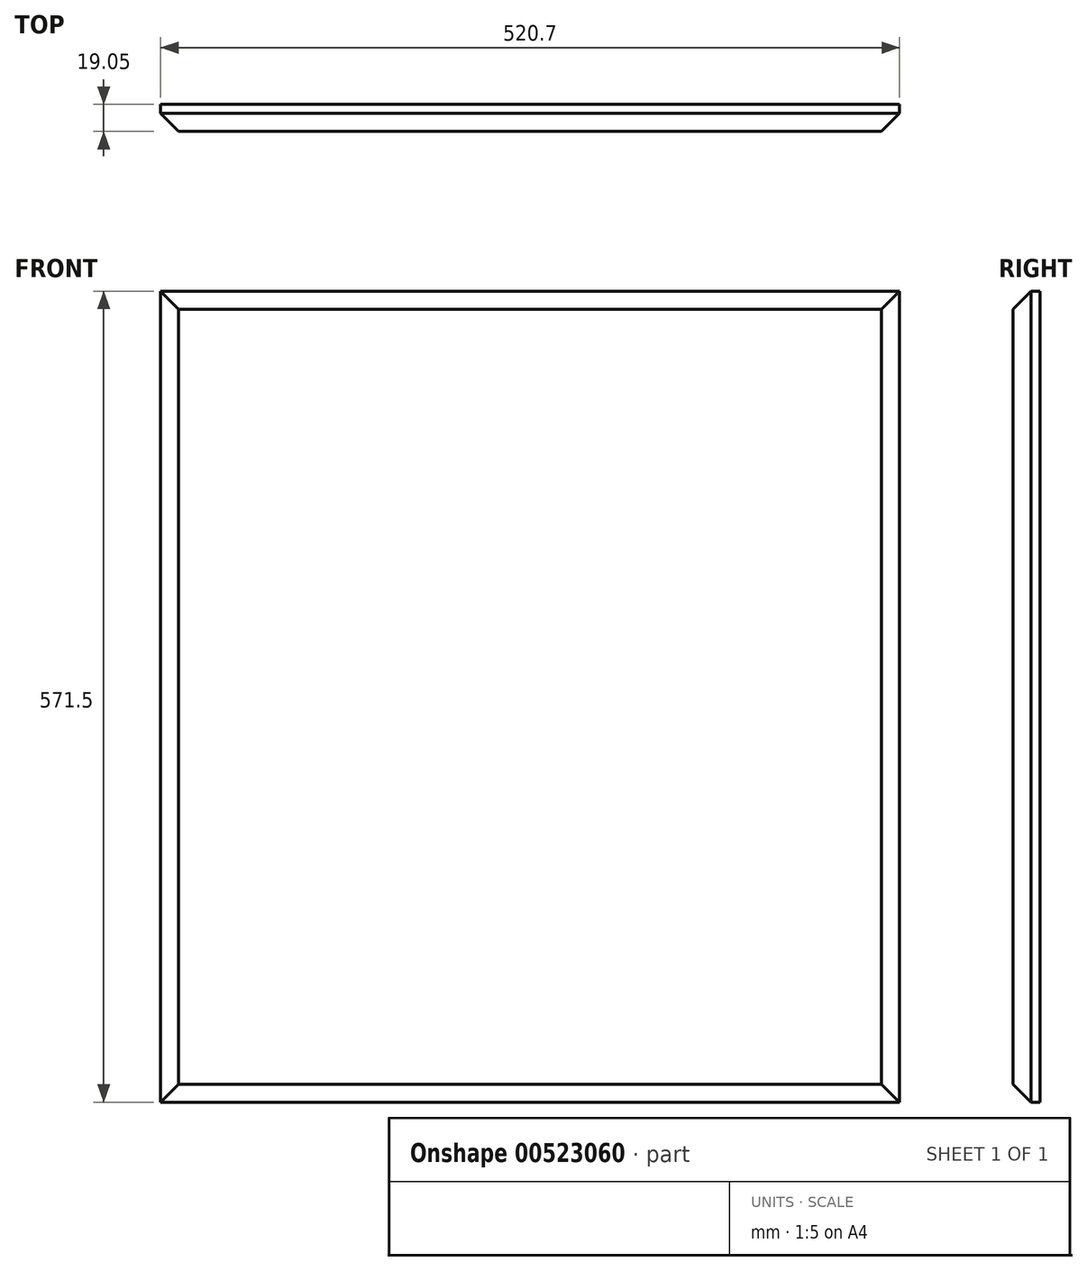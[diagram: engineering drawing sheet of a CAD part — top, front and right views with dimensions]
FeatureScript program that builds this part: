
annotation { "Feature Type Name" : "Feature", "Feature Type Description" : "" }
export const myFeature = defineFeature(function(context is Context, id is Id, definition is map)
    precondition{}
    {
        {
            var Q0;
            Q0=qCreatedBy(makeId("Front.planeOp"),FACE);
            var sketch = newSketch(context, id + "F0", { "sketchPlane" : qUnion([Q0])});
            skLineSegment(sketch, "E0.bottom", {"start": v(0, 0) * mm, "end": v(520.7, 0) * mm});
            skLineSegment(sketch, "E0.top", {"start": v(0, 571.5) * mm, "end": v(520.7, 571.5) * mm});
            skLineSegment(sketch, "E0.left", {"start": v(0, 0) * mm, "end": v(0, 571.5) * mm});
            skLineSegment(sketch, "E0.right", {"start": v(520.7, 0) * mm, "end": v(520.7, 571.5) * mm});
            skSolve(sketch);
        }
        {
            var Q0;
            Q0=qSketchRegion(id+"F0",true);
            extrude(context, id + "F1", {"entities" : qUnion([Q0]), "depth" : 19.05 * mm, "offsetDistance" : 25.4 * mm});
        }
        {
            var Q0;
            Q0=makeQuery(id+"F1.opExtrude","CAP_FACE",FACE,{"disambiguationData":[OSD([sQuery(id+"F0.wireOp",EDGE,"E0.bottom"),sQuery(id+"F0.wireOp",EDGE,"E0.top"),sQuery(id+"F0.wireOp",EDGE,"E0.left"),sQuery(id+"F0.wireOp",EDGE,"E0.right")])],"isStart":false});
            chamfer(context, id + "F2", {"entities" : qUnion([Q0]), "width" : 12.7 * mm, "tangentPropagation" : true});
        }
    });
